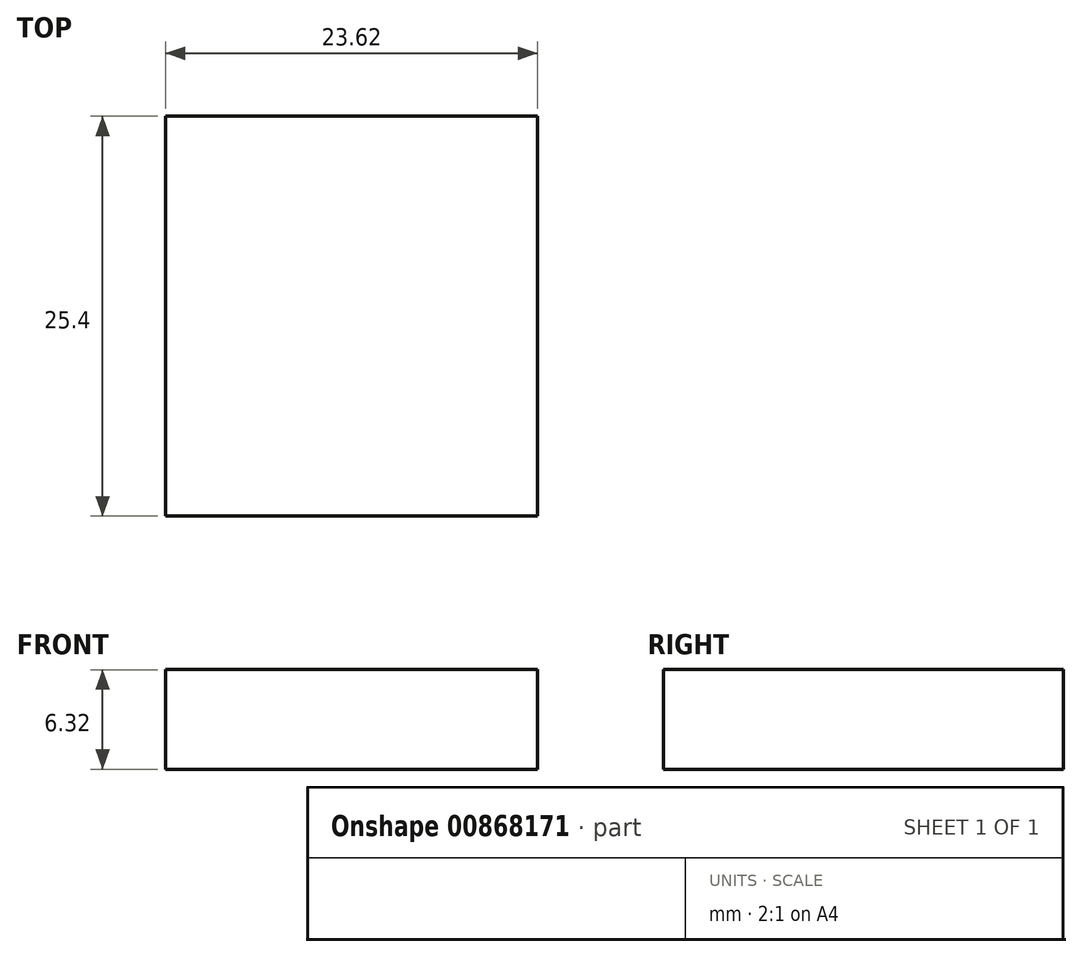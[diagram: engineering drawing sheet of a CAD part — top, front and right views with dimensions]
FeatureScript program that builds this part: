
annotation { "Feature Type Name" : "Feature", "Feature Type Description" : "" }
export const myFeature = defineFeature(function(context is Context, id is Id, definition is map)
    precondition{}
    {
        {
            var Q0;
            Q0=qCreatedBy(makeId("Front.planeOp"),FACE);
            var sketch = newSketch(context, id + "F0", { "sketchPlane" : qUnion([Q0])});
            skLineSegment(sketch, "E0.bottom", {"start": v(-63.61, 0) * mm, "end": v(-39.99, 0) * mm});
            skLineSegment(sketch, "E0.top", {"start": v(-63.61, 6.32) * mm, "end": v(-39.99, 6.32) * mm});
            skLineSegment(sketch, "E0.left", {"start": v(-63.61, 0) * mm, "end": v(-63.61, 6.32) * mm});
            skLineSegment(sketch, "E0.right", {"start": v(-39.99, 0) * mm, "end": v(-39.99, 6.32) * mm});
            skSolve(sketch);
        }
        {
            var Q0;
            Q0 = qSketchRegion(id + "F0", true);
            extrude(context, id + "F1", {"entities" : qUnion([Q0]), "depth" : 25.4 * mm, "offsetDistance" : 25.4 * mm});
        }
    });
